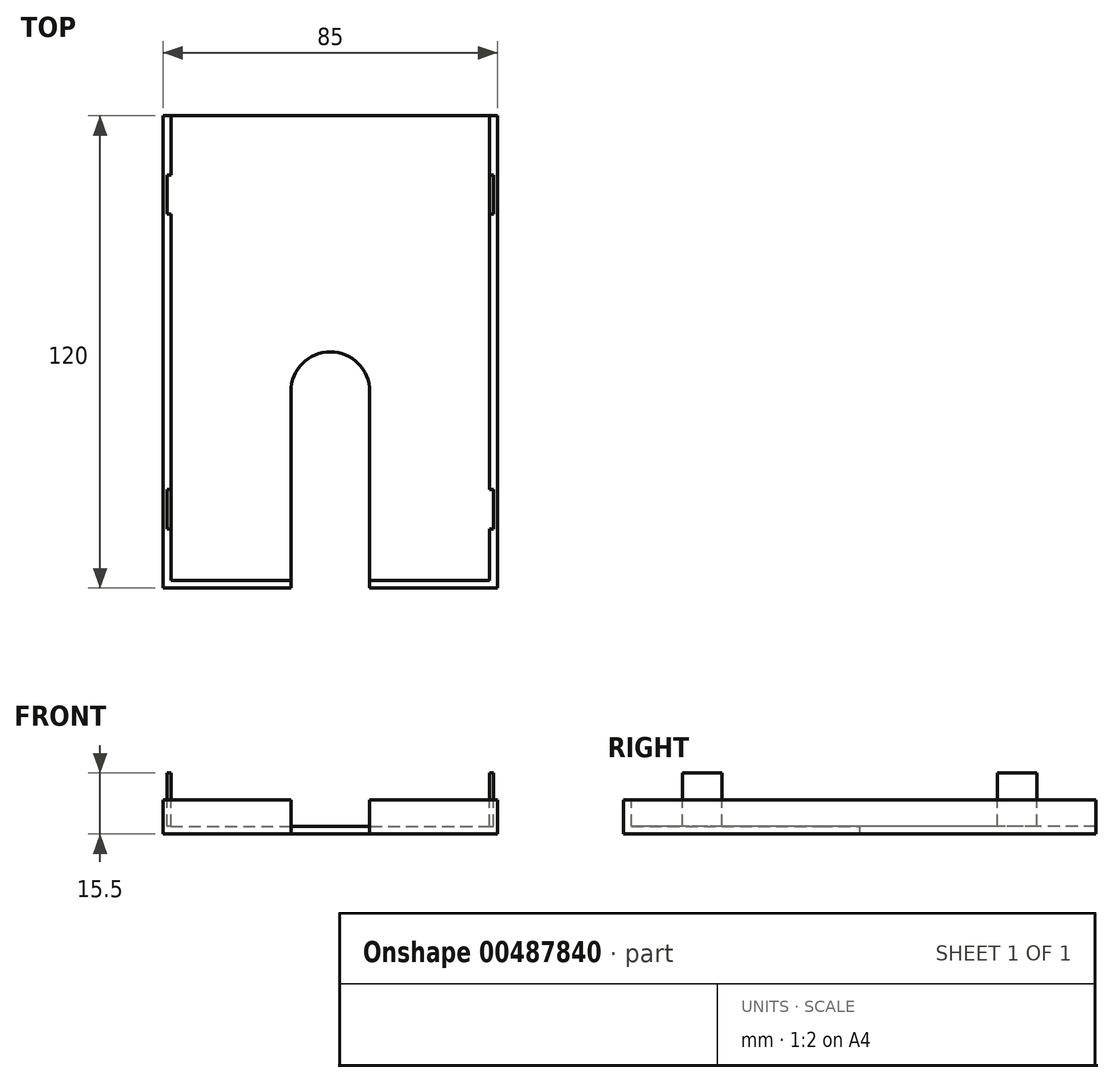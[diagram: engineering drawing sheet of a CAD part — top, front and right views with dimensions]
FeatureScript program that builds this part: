
annotation { "Feature Type Name" : "Feature", "Feature Type Description" : "" }
export const myFeature = defineFeature(function(context is Context, id is Id, definition is map)
    precondition{}
    {
        {
            var Q0;
            Q0=qCreatedBy(makeId("Top.planeOp"),FACE);
            var sketch = newSketch(context, id + "F0", { "sketchPlane" : qUnion([Q0])});
            skLineSegment(sketch, "E0.bottom", {"start": v(-42.5, 60) * mm, "end": v(42.5, 60) * mm});
            skLineSegment(sketch, "E0.top", {"start": v(-42.5, -60) * mm, "end": v(42.5, -60) * mm});
            skLineSegment(sketch, "E0.left", {"start": v(-42.5, 60) * mm, "end": v(-42.5, -60) * mm});
            skLineSegment(sketch, "E0.right", {"start": v(42.5, 60) * mm, "end": v(42.5, -60) * mm});
            skSolve(sketch);
        }
        {
            var Q0;
            Q0 = qSketchRegion(id + "F0", true);
            extrude(context, id + "F1", {"entities" : qUnion([Q0]), "depth" : 8.75 * mm});
        }
        {
            var Q0;
            Q0=makeQuery(id+"F1.opExtrude","CAP_FACE",FACE,{"disambiguationData":[OSD([sQuery(id+"F0.wireOp",EDGE,"E0.bottom"),sQuery(id+"F0.wireOp",EDGE,"E0.top"),sQuery(id+"F0.wireOp",EDGE,"E0.left"),sQuery(id+"F0.wireOp",EDGE,"E0.right")])],"isStart":false});
            var sketch = newSketch(context, id + "F2", { "sketchPlane" : qUnion([Q0])});
            skLineSegment(sketch, "E1.bottom", {"start": v(-40.5, 60) * mm, "end": v(40.5, 60) * mm});
            skLineSegment(sketch, "E1.top", {"start": v(-40.5, -58) * mm, "end": v(40.5, -58) * mm});
            skLineSegment(sketch, "E1.left", {"start": v(-40.5, 60) * mm, "end": v(-40.5, -58) * mm});
            skLineSegment(sketch, "E1.right", {"start": v(40.5, 60) * mm, "end": v(40.5, -58) * mm});
            skSolve(sketch);
        }
        {
            var Q0;
            Q0 = qSketchRegion(id + "F2", true);
            extrude(context, id + "F3", {"entities" : qUnion([Q0]), "operationType" : NewBodyOperationType.REMOVE, "oppositeDirection" : true, "depth" : 6.75 * mm});
        }
        {
            var Q0;
            Q0=makeQuery(id+"F1.opExtrude","CAP_FACE",FACE,{"disambiguationData":[OSD([sQuery(id+"F0.wireOp",EDGE,"E0.bottom"),sQuery(id+"F0.wireOp",EDGE,"E0.top"),sQuery(id+"F0.wireOp",EDGE,"E0.left"),sQuery(id+"F0.wireOp",EDGE,"E0.right")])],"isStart":false});
            var sketch = newSketch(context, id + "F4", { "sketchPlane" : qUnion([Q0])});
            skLineSegment(sketch, "E2.bottom", {"start": v(-10, -60) * mm, "end": v(10, -60) * mm});
            skLineSegment(sketch, "E2.left", {"start": v(-10, -60) * mm, "end": v(-10, -10) * mm});
            skLineSegment(sketch, "E2.right", {"start": v(10, -60) * mm, "end": v(10, -10) * mm});
            skArc(sketch, "E3", {"start": v(10, -10) * mm, "mid": v(0, 0) * mm, "end": v(-10, -10) * mm});
            skSolve(sketch);
        }
        {
            var Q0;
            Q0 = qSketchRegion(id + "F4", true);
            extrude(context, id + "F5", {"entities" : qUnion([Q0]), "operationType" : NewBodyOperationType.REMOVE, "oppositeDirection" : true, "depth" : 25 * mm});
        }
        {
            var Q0;
            {var subQ0=sQuery(id+"F0.wireOp",EDGE,"E0.left");var subQ1=sQuery(id+"F0.wireOp",EDGE,"E0.top");var subQ2=sQuery(id+"F0.wireOp",EDGE,"E0.bottom");Q0=makeQuery(id+"F5.boolean.opBoolean","SPLIT",FACE,{"disambiguationData":[TD([makeQuery(id+"F1.opExtrude","SWEPT_FACE",FACE,{"disambiguationData":[OSD([subQ0])]})])],"derivedFrom":makeQuery(id+"F1.opExtrude","CAP_FACE",FACE,{"disambiguationData":[OSD([subQ2,subQ1,subQ0,sQuery(id+"F0.wireOp",EDGE,"E0.right")])],"isStart":false})});}
            var sketch = newSketch(context, id + "F6", { "sketchPlane" : qUnion([Q0])});
            skPoint(sketch, "E4.oppositeSnap0", {"position": v(-41.5, 60) * mm});
            skLineSegment(sketch, "E4.bottom", {"start": v(-40.5, 45) * mm, "end": v(-41.5, 45) * mm});
            skLineSegment(sketch, "E4.top", {"start": v(-40.5, 35) * mm, "end": v(-41.5, 35) * mm});
            skLineSegment(sketch, "E4.left", {"start": v(-40.5, 45) * mm, "end": v(-40.5, 35) * mm});
            skLineSegment(sketch, "E4.right", {"start": v(-41.5, 45) * mm, "end": v(-41.5, 35) * mm});
            skSolve(sketch);
        }
        {
            var Q0;
            Q0 = qSketchRegion(id + "F6", true);
            extrude(context, id + "F7", {"entities" : qUnion([Q0]), "operationType" : NewBodyOperationType.REMOVE, "oppositeDirection" : true, "depth" : 6.75 * mm});
        }
        {
            var Q0;
            {var subQ0=sQuery(id+"F0.wireOp",EDGE,"E0.top");var subQ1=sQuery(id+"F0.wireOp",EDGE,"E0.right");var subQ2=sQuery(id+"F0.wireOp",EDGE,"E0.bottom");Q0=makeQuery(id+"F5.boolean.opBoolean","SPLIT",FACE,{"disambiguationData":[TD([makeQuery(id+"F1.opExtrude","SWEPT_FACE",FACE,{"disambiguationData":[OSD([subQ1])]})])],"derivedFrom":makeQuery(id+"F1.opExtrude","CAP_FACE",FACE,{"disambiguationData":[OSD([subQ2,subQ0,sQuery(id+"F0.wireOp",EDGE,"E0.left"),subQ1])],"isStart":false})});}
            var sketch = newSketch(context, id + "F8", { "sketchPlane" : qUnion([Q0])});
            skLineSegment(sketch, "E5.bottom", {"start": v(40.5, -35) * mm, "end": v(41.5, -35) * mm});
            skLineSegment(sketch, "E5.top", {"start": v(40.5, -45) * mm, "end": v(41.5, -45) * mm});
            skLineSegment(sketch, "E5.left", {"start": v(40.5, -35) * mm, "end": v(40.5, -45) * mm});
            skLineSegment(sketch, "E5.right", {"start": v(41.5, -35) * mm, "end": v(41.5, -45) * mm});
            skSolve(sketch);
        }
        {
            var Q0;
            Q0 = qSketchRegion(id + "F8", true);
            extrude(context, id + "F9", {"entities" : qUnion([Q0]), "operationType" : NewBodyOperationType.REMOVE, "oppositeDirection" : true, "depth" : 6.75 * mm});
        }
        {
            var Q0;
            {var subQ0=sQuery(id+"F0.wireOp",EDGE,"E0.left");var subQ1=sQuery(id+"F0.wireOp",EDGE,"E0.top");var subQ2=sQuery(id+"F0.wireOp",EDGE,"E0.bottom");Q0=makeQuery(id+"F5.boolean.opBoolean","SPLIT",FACE,{"disambiguationData":[TD([makeQuery(id+"F1.opExtrude","SWEPT_FACE",FACE,{"disambiguationData":[OSD([subQ0])]})])],"derivedFrom":makeQuery(id+"F1.opExtrude","CAP_FACE",FACE,{"disambiguationData":[OSD([subQ2,subQ1,subQ0,sQuery(id+"F0.wireOp",EDGE,"E0.right")])],"isStart":false})});}
            var sketch = newSketch(context, id + "F10", { "sketchPlane" : qUnion([Q0])});
            skLineSegment(sketch, "E6.bottom", {"start": v(-40.5, -45) * mm, "end": v(-41.5, -45) * mm});
            skLineSegment(sketch, "E6.top", {"start": v(-40.5, -35) * mm, "end": v(-41.5, -35) * mm});
            skLineSegment(sketch, "E6.left", {"start": v(-40.5, -45) * mm, "end": v(-40.5, -35) * mm});
            skLineSegment(sketch, "E6.right", {"start": v(-41.5, -45) * mm, "end": v(-41.5, -35) * mm});
            skSolve(sketch);
        }
        {
            var Q0;
            Q0 = qSketchRegion(id + "F10", true);
            extrude(context, id + "F11", {"entities" : qUnion([Q0]), "operationType" : NewBodyOperationType.ADD, "depth" : 6.75 * mm});
        }
        {
            var Q0;
            {var subQ0=sQuery(id+"F0.wireOp",EDGE,"E0.top");var subQ1=sQuery(id+"F0.wireOp",EDGE,"E0.right");var subQ2=sQuery(id+"F0.wireOp",EDGE,"E0.bottom");Q0=makeQuery(id+"F5.boolean.opBoolean","SPLIT",FACE,{"disambiguationData":[TD([makeQuery(id+"F1.opExtrude","SWEPT_FACE",FACE,{"disambiguationData":[OSD([subQ1])]})])],"derivedFrom":makeQuery(id+"F1.opExtrude","CAP_FACE",FACE,{"disambiguationData":[OSD([subQ2,subQ0,sQuery(id+"F0.wireOp",EDGE,"E0.left"),subQ1])],"isStart":false})});}
            var sketch = newSketch(context, id + "F12", { "sketchPlane" : qUnion([Q0])});
            skLineSegment(sketch, "E7.bottom", {"start": v(40.5, 45) * mm, "end": v(41.5, 45) * mm});
            skLineSegment(sketch, "E7.top", {"start": v(40.5, 35) * mm, "end": v(41.5, 35) * mm});
            skLineSegment(sketch, "E7.left", {"start": v(40.5, 45) * mm, "end": v(40.5, 35) * mm});
            skLineSegment(sketch, "E7.right", {"start": v(41.5, 45) * mm, "end": v(41.5, 35) * mm});
            skSolve(sketch);
        }
        {
            var Q0;
            Q0 = qSketchRegion(id + "F12", true);
            extrude(context, id + "F13", {"entities" : qUnion([Q0]), "operationType" : NewBodyOperationType.ADD, "depth" : 6.75 * mm});
        }
    });
